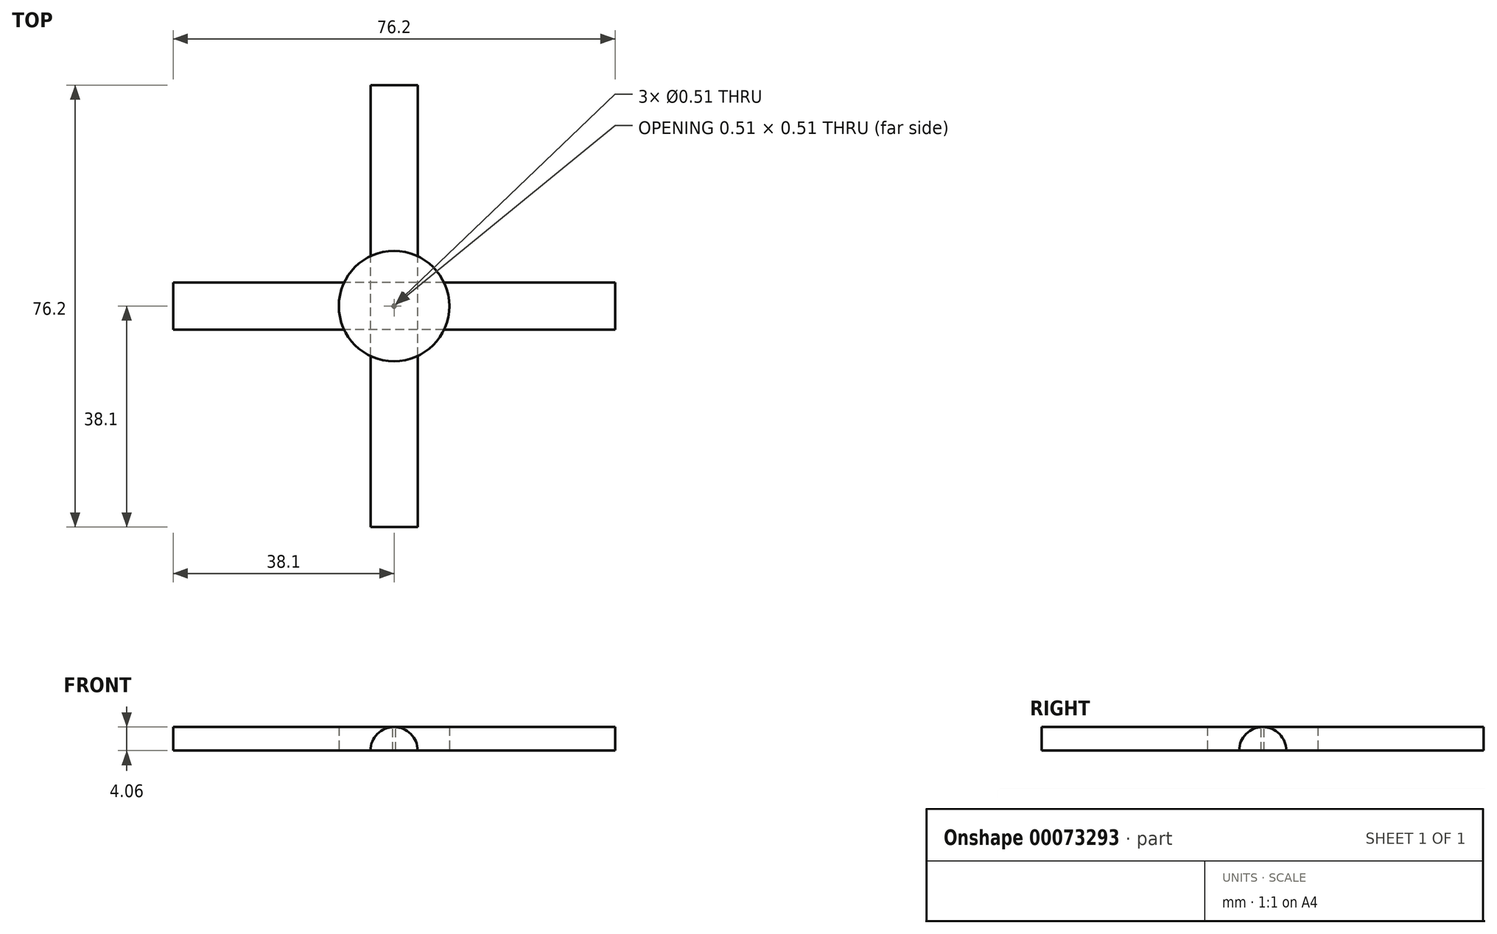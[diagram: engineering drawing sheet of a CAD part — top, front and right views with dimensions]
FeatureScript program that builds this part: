
annotation { "Feature Type Name" : "Feature", "Feature Type Description" : "" }
export const myFeature = defineFeature(function(context is Context, id is Id, definition is map)
    precondition{}
    {
        {
            var Q0;
            Q0=qCreatedBy(makeId("Top.planeOp"),FACE);
            var sketch = newSketch(context, id + "F0", { "sketchPlane" : qUnion([Q0])});
            skCircle(sketch, "E0", {"center": v(0, 0) * mm, "radius": 9.53 * mm});
            skSolve(sketch);
        }
        {
            var Q0;
            Q0=qCreatedBy(makeId("Right.planeOp"),FACE);
            var sketch = newSketch(context, id + "F1", { "sketchPlane" : qUnion([Q0])});
            skArc(sketch, "E1", {"start": v(4.06, 0) * mm, "mid": v(0, 4.06) * mm, "end": v(-4.06, 0) * mm});
            skLineSegment(sketch, "E2", {"start": v(4.06, 0) * mm, "end": v(-4.06, 0) * mm});
            skSolve(sketch);
        }
        {
            var Q0;
            Q0=qCreatedBy(makeId("Front.planeOp"),FACE);
            var sketch = newSketch(context, id + "F2", { "sketchPlane" : qUnion([Q0])});
            skArc(sketch, "E3", {"start": v(-4.06, 0) * mm, "mid": v(0, 4.06) * mm, "end": v(4.06, 0) * mm});
            skLineSegment(sketch, "E4", {"start": v(4.06, 0) * mm, "end": v(-4.06, 0) * mm});
            skSolve(sketch);
        }
        {
            var Q0;
            Q0 = qSketchRegion(id + "F2", true);
            extrude(context, id + "F3", {"entities" : qUnion([Q0]), "endBound" : BoundingType.SYMMETRIC, "depth" : 76.2 * mm});
        }
        {
            var Q0;
            Q0=makeQuery(id+"F1.imprint","IMPRINT",FACE,{"disambiguationData":[TD([[makeQuery(id+"F1.imprint","IMPRINT",EDGE,{"derivedFrom":sQuery(id+"F1.wireOp",EDGE,"E1")}),1.0]])]});
            var Q1;
            Q1=sQuery(id+"F1.wireOp",EDGE,"E1");
            extrude(context, id + "F4", {"entities" : qUnion([Q0]), "surfaceEntities" : qUnion([Q1]), "endBound" : BoundingType.SYMMETRIC, "depth" : 76.2 * mm});
        }
        {
            var Q0;
            Q0=makeQuery(id+"F0.imprint","IMPRINT",FACE,{"disambiguationData":[TD([[makeQuery(id+"F0.imprint","IMPRINT",EDGE,{"derivedFrom":sQuery(id+"F0.wireOp",EDGE,"E0")}),1.0]])]});
            var Q1;
            Q1=sQuery(id+"F0.wireOp",EDGE,"E0");
            extrude(context, id + "F5", {"entities" : qUnion([Q0]), "surfaceEntities" : qUnion([Q1]), "depth" : 4.06 * mm});
        }
        {
            var Q0;
            Q0=makeQuery(id+"F5.opExtrude","CAP_FACE",FACE,{"disambiguationData":[OSD([sQuery(id+"F0.wireOp",EDGE,"E0")])],"isStart":false});
            var sketch = newSketch(context, id + "F6", { "sketchPlane" : qUnion([Q0])});
            skCircle(sketch, "E5", {"center": v(0, 0) * mm, "radius": 0.25 * mm});
            skSolve(sketch);
        }
        {
            var Q0;
            Q0=makeQuery(id+"F6.imprint","IMPRINT",FACE,{"disambiguationData":[TD([[makeQuery(id+"F6.imprint","IMPRINT",EDGE,{"derivedFrom":sQuery(id+"F6.wireOp",EDGE,"E5")}),1.0]])]});
            extrude(context, id + "F7", {"entities" : qUnion([Q0]), "operationType" : NewBodyOperationType.REMOVE, "oppositeDirection" : true, "depth" : 25.4 * mm});
        }
    });
